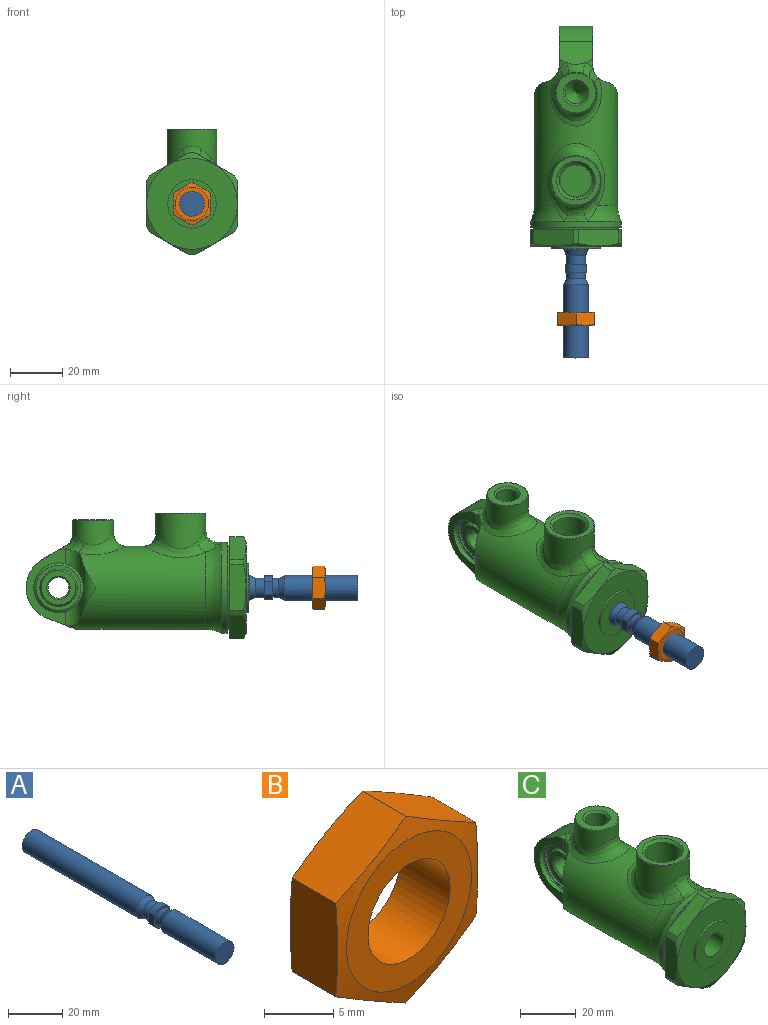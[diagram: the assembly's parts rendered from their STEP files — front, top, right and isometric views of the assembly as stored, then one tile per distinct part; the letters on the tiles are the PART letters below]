
ASSEMBLY  parts=3 mates=1
PART A: 14 faces, bbox 9.5x100.7x9.5 mm
  f0: cylinder r=4.76mm len=59.27mm, axis (0,-1,0), area 1773.6mm2, adj f4,f11
  f1: cylinder r=4.57mm len=7.8mm, axis (0,-1,0), area 28.9mm2, adj f2,f7,f8,f12
  f2: plane 9.14x7.8mm, normal (0,1,0), area 18.7mm2, adj f1,f3,f7,f8,f13
  f3: cylinder r=3.68mm len=7.37mm, axis (0,-1,0), area 81.8mm2, adj f2,f4
  f4: cone r=4.76mm half-angle=25deg, axis (0,1,0), area 67.7mm2, adj f0,f3
  f5: plane 9.53x9.53mm, normal (0,-1,0), area 71.3mm2, adj f6
  f6: cylinder r=4.76mm len=28.19mm, axis (0,-1,0), area 843.6mm2, adj f5,f9
  f7: plane 4.78x3.1mm, normal (1,0,0), area 14.8mm2, adj f1,f2,f12,f13
  f8: plane 4.78x3.1mm, normal (-1,0,0), area 14.8mm2, adj f1,f2,f12,f13
  f9: cone r=3.68mm half-angle=25.3deg, axis (0,-1,0), area 66.9mm2, adj f6,f10
  f10: cylinder r=3.68mm len=7.37mm, axis (0,-1,0), area 47mm2, adj f9,f12
  f11: plane 9.53x9.53mm, normal (0,1,0), area 71.3mm2, adj f0
  f12: plane 9.14x7.8mm, normal (0,-1,0), area 18.7mm2, adj f1,f7,f8,f10,f13
  f13: cylinder r=4.57mm len=7.8mm, axis (0,-1,0), area 28.9mm2, adj f2,f7,f8,f12
PART B: 11 faces, bbox 17.1x5.7x17.1 mm
  f0: cone r=10.16mm half-angle=80deg, axis (0,1,0), area 49.6mm2, adj f1,f5,f6,f7,f8,f9,f10
  f1: plane 7.15x4.84mm, normal (0.5,0,0.87), area 38.7mm2, adj f0,f4,f8,f9
  f2: cylinder r=4.19mm len=8.38mm, axis (0,-1,0), area 133.7mm2, adj f3,f7
  f3: plane 13.02x13.02mm, normal (0,1,0), area 77.9mm2, adj f2,f4
  f4: cone r=6.38mm half-angle=80deg, axis (0,-1,0), area 46.1mm2, adj f1,f3,f5,f6,f8,f9,f10
  f5: plane 8.25x4.84mm, normal (-1,0,0), area 38.8mm2, adj f0,f4,f6,f8
  f6: plane 7.15x4.84mm, normal (-0.5,0,-0.87), area 38.8mm2, adj f0,f4,f5,f10
  f7: plane 12.76x12.76mm, normal (0,-1,0), area 72.8mm2, adj f0,f2
  f8: plane 7.15x4.84mm, normal (-0.5,0,0.87), area 38.7mm2, adj f0,f1,f4,f5
  f9: plane 8.85x5.44mm, normal (1,0,0), area 38.8mm2, adj f0,f1,f4,f10
  f10: plane 7.15x4.84mm, normal (0.5,0,-0.87), area 38.7mm2, adj f0,f4,f6,f9
PART C: 84 faces, bbox 42.9x85.7x50.3 mm
  f0: cone r=3.97mm half-angle=45deg, axis (-1,0,0), area 19.1mm2, adj f1,f2
  f1: cylinder r=3.97mm len=8.51mm, axis (1,0,0), area 212.2mm2, adj f0,f58
  f2: plane 13.16x13.16mm, normal (-1,0,0), area 73.1mm2, adj f0,f59
  f3: cylinder r=4.76mm len=60mm, axis (0,1,0), area 1795.4mm2, adj f10,f15
  f4: plane 17.62x6.32mm, normal (-1,0,0), area 105.5mm2, adj f12,f13,f18,f80
  f5: cylinder r=9.53mm len=19.05mm, axis (0,0,1), area 616.9mm2, adj f64,f68,f69,f70,f83
  f6: cylinder r=5.08mm len=21.39mm, axis (0,0,1), area 74.6mm2, adj f29,f36,f46,f48,f50
  f7: cylinder r=15.88mm len=3.71mm, axis (0,-1,0), area 5.1mm2, adj f9,f33,f40,f73
  f8: cylinder r=9.59mm len=19.18mm, axis (1,0,0), area 175.8mm2, adj f9,f31,f32,f33,f82
  f9: cylinder r=6.6mm len=11.33mm, axis (0,0,1), area 64.3mm2, adj f7,f8,f31,f33,f50,f74
  f10: plane 9.53x9.53mm, normal (0,-1,0), area 71.3mm2, adj f3
  f11: cylinder r=19.56mm len=5.34mm, axis (0,-1,0), area 11.8mm2, adj f18,f77,f80,f81
  f12: cylinder r=19.56mm len=5.34mm, axis (0,-1,0), area 11.8mm2, adj f4,f18,f77,f80
  f13: cylinder r=19.56mm len=5.34mm, axis (0,-1,0), area 11.8mm2, adj f4,f18,f44,f80
  f14: cylinder r=19.56mm len=5.34mm, axis (0,-1,0), area 11.8mm2, adj f18,f44,f61,f80
  f15: plane 18.54x18.54mm, normal (0,-1,0), area 198.8mm2, adj f3,f45
  f16: plane 34.29x34.29mm, normal (0,-1,0), area 86.5mm2, adj f17,f26
  f17: cylinder r=16.32mm len=32.64mm, axis (0,-1,0), area 65.1mm2, adj f16,f18
  f18: plane 39.12x34.93mm, normal (0,1,0), area 215.4mm2, adj f4,f11,f12,f13,f14,f17,f44,f61
  f19: cone r=8.6mm half-angle=50.6deg, axis (1,0,0), area 68mm2, adj f42,f60
  f20: plane 12x12mm, normal (0,0,1), area 113.1mm2, adj f67
  f21: cone r=4.19mm half-angle=37deg, axis (0,0,1), area 91.6mm2, adj f22
  f22: cylinder r=4.19mm len=8.38mm, axis (0,0,1), area 193.9mm2, adj f21,f65
  f23: cylinder r=15.88mm len=3.71mm, axis (0,-1,0), area 5.1mm2, adj f40,f47,f48,f71
  f24: torus R=28.57mm, axis (0,1,0), area 565.2mm2, adj f25,f50,f68,f70
  f25: cylinder r=17.4mm len=34.8mm, axis (0,-1,0), area 249.9mm2, adj f24,f26,f69
  f26: cone r=17.4mm half-angle=45deg, axis (0,1,0), area 39mm2, adj f16,f25
  f27: plane 18.54x18.54mm, normal (0,0,1), area 98.2mm2, adj f64,f66
  f28: plane 15.24x15.24mm, normal (0,0,1), area 105.4mm2, adj f63,f65
  f29: plane 0.18x0mm, normal (0,1,0), area 0mm2, adj f6,f50
  f30: plane 0.18x0mm, normal (0,1,0), area 0mm2, adj f31,f50
  f31: cylinder r=5.08mm len=21.39mm, axis (0,0,1), area 73.5mm2, adj f8,f9,f30,f32,f50
  f32: cylinder r=6.6mm len=11.31mm, axis (0,0,1), area 62.5mm2, adj f8,f31,f33,f41,f50
  f33: plane 28.86x14.99mm, normal (1,0,0), area 128.8mm2, adj f7,f8,f9,f32,f39,f40,f41
  f34: plane 20.19x20.19mm, normal (-1,0,0), area 35.5mm2, adj f35,f42
  f35: cylinder r=10.1mm len=20.19mm, axis (1,0,0), area 65.3mm2, adj f34,f37
  f36: cylinder r=9.52mm len=19.04mm, axis (1,0,0), area 173.3mm2, adj f6,f37,f46,f47,f48
  f37: plane 20.19x20.19mm, normal (1,0,0), area 35.5mm2, adj f35,f36
  f38: cylinder r=6.38mm len=12.76mm, axis (0,0,1), area 453.1mm2, adj f66,f67
  f39: cylinder r=12.45mm len=22.29mm, axis (-1,0,0), area 353.1mm2, adj f33,f40,f41,f47
  f40: plane 13.22x9.19mm, normal (0,0.52,0.86), area 117.7mm2, adj f7,f23,f33,f39,f47,f72
  f41: plane 12.76x11.09mm, normal (0,0.36,-0.93), area 135.4mm2, adj f32,f33,f39,f46,f47,f50
  f42: cylinder r=9.52mm len=19.04mm, axis (1,0,0), area 50mm2, adj f19,f34
  f43: plane 34.8x34.8mm, normal (0,-1,0), area 681mm2, adj f45,f80
  f44: plane 15.26x8.81mm, normal (-0.5,0,0.87), area 105.5mm2, adj f13,f14,f18,f80
  f45: cylinder r=9.27mm len=18.54mm, axis (0,-1,0), area 59.2mm2, adj f15,f43
  f46: cylinder r=6.6mm len=11.52mm, axis (0,0,1), area 63.4mm2, adj f6,f36,f41,f47,f50
  f47: plane 28.86x14.99mm, normal (-1,0,0), area 131.2mm2, adj f23,f36,f39,f40,f41,f46,f48
  f48: cylinder r=6.6mm len=11.53mm, axis (0,0,1), area 65.6mm2, adj f6,f23,f36,f47,f50,f76
  f49: cylinder r=7.87mm len=15.75mm, axis (0,0,1), area 359.4mm2, adj f63,f71,f72,f73,f74,f75,f76
  f50: cylinder r=15.88mm len=53.06mm, axis (0,-1,0), area 3913.9mm2, adj f6,f9,f24,f29,f30,f31,f32,f41
  f51: cylinder r=10.1mm len=20.19mm, axis (1,0,0), area 65.3mm2, adj f52,f82
  f52: plane 20.19x20.19mm, normal (1,0,0), area 35.5mm2, adj f51,f53
  f53: cylinder r=9.52mm len=19.04mm, axis (1,0,0), area 49.9mm2, adj f52,f54
  f54: cone r=9.53mm half-angle=50.6deg, axis (-1,0,0), area 68mm2, adj f53,f55
  f55: plane 17.2x17.2mm, normal (1,0,0), area 71.9mm2, adj f54,f56
  f56: revolved ~14.29x14.29mm, area 57.6mm2, adj f55,f57
  f57: plane 13.16x13.16mm, normal (1,0,0), area 73.1mm2, adj f56,f58
  f58: cone r=4.48mm half-angle=45deg, axis (1,0,0), area 19.1mm2, adj f1,f57
  f59: revolved ~14.29x14.29mm, area 57.6mm2, adj f2,f60
  f60: plane 17.2x17.2mm, normal (-1,0,0), area 71.9mm2, adj f19,f59
  f61: plane 15.26x8.81mm, normal (0.5,0,0.87), area 105.4mm2, adj f14,f18,f78,f80
  f62: plane 17.62x6.32mm, normal (1,0,0), area 105.5mm2, adj f18,f78,f79,f80
  f63: cone r=7.87mm half-angle=45deg, axis (0,0,-1), area 17.5mm2, adj f28,f49
  f64: cone r=9.27mm half-angle=45deg, axis (0,0,-1), area 21.2mm2, adj f5,f27
  f65: cone r=4.95mm half-angle=45deg, axis (0,0,1), area 30.9mm2, adj f22,f28
  f66: cone r=7.4mm half-angle=45deg, axis (0,0,1), area 62.2mm2, adj f27,f38
  f67: torus R=6mm, axis (0,0,-1), area 23.5mm2, adj f20,f38
  f68: bspline ~9.19x7.34mm, area 45.6mm2, adj f5,f24,f69,f83
  f69: bspline ~8.76x7.42mm, area 60.3mm2, adj f5,f25,f68,f70
  f70: bspline ~9.19x7.34mm, area 45.6mm2, adj f5,f24,f69,f83
  f71: bspline ~5.8x5.58mm, area 20.2mm2, adj f23,f49,f72,f76
  f72: bspline ~7.44x4.91mm, area 37.2mm2, adj f40,f49,f71,f73
  f73: bspline ~5.8x5.58mm, area 20.2mm2, adj f7,f49,f72,f74
  f74: bspline ~5.96x5.6mm, area 19.5mm2, adj f9,f49,f73,f75
  f75: bspline ~19.45x18.25mm, area 215.2mm2, adj f49,f50,f74,f76
  f76: bspline ~5.96x5.6mm, area 19.5mm2, adj f48,f49,f71,f75
  f77: plane 15.26x8.81mm, normal (-0.5,0,-0.87), area 105.5mm2, adj f11,f12,f18,f80
  f78: cylinder r=19.56mm len=5.34mm, axis (0,-1,0), area 11.8mm2, adj f18,f61,f62,f80
  f79: cylinder r=19.56mm len=5.34mm, axis (0,-1,0), area 11.8mm2, adj f18,f62,f80,f81
  f80: cone r=19.56mm half-angle=65deg, axis (0,1,0), area 111.8mm2, adj f4,f11,f12,f13,f14,f43,f44,f61
  f81: plane 15.26x8.81mm, normal (0.5,0,-0.87), area 105.4mm2, adj f11,f18,f79,f80
  f82: plane 20.19x20.19mm, normal (-1,0,0), area 31.4mm2, adj f8,f51
  f83: bspline ~23.76x21.99mm, area 274.7mm2, adj f5,f50,f68,f70
PLACE A rot(axis=(0,-1,0.03),0deg) t=(0,29,0)mm
PLACE B rot(axis=(0,-1,0.03),0deg) t=(0,29,0)mm
PLACE C at identity fixed
MATE slider A.f0 <-> C.f3  axis (0,1,0) through (0,-13.77,0)mm
